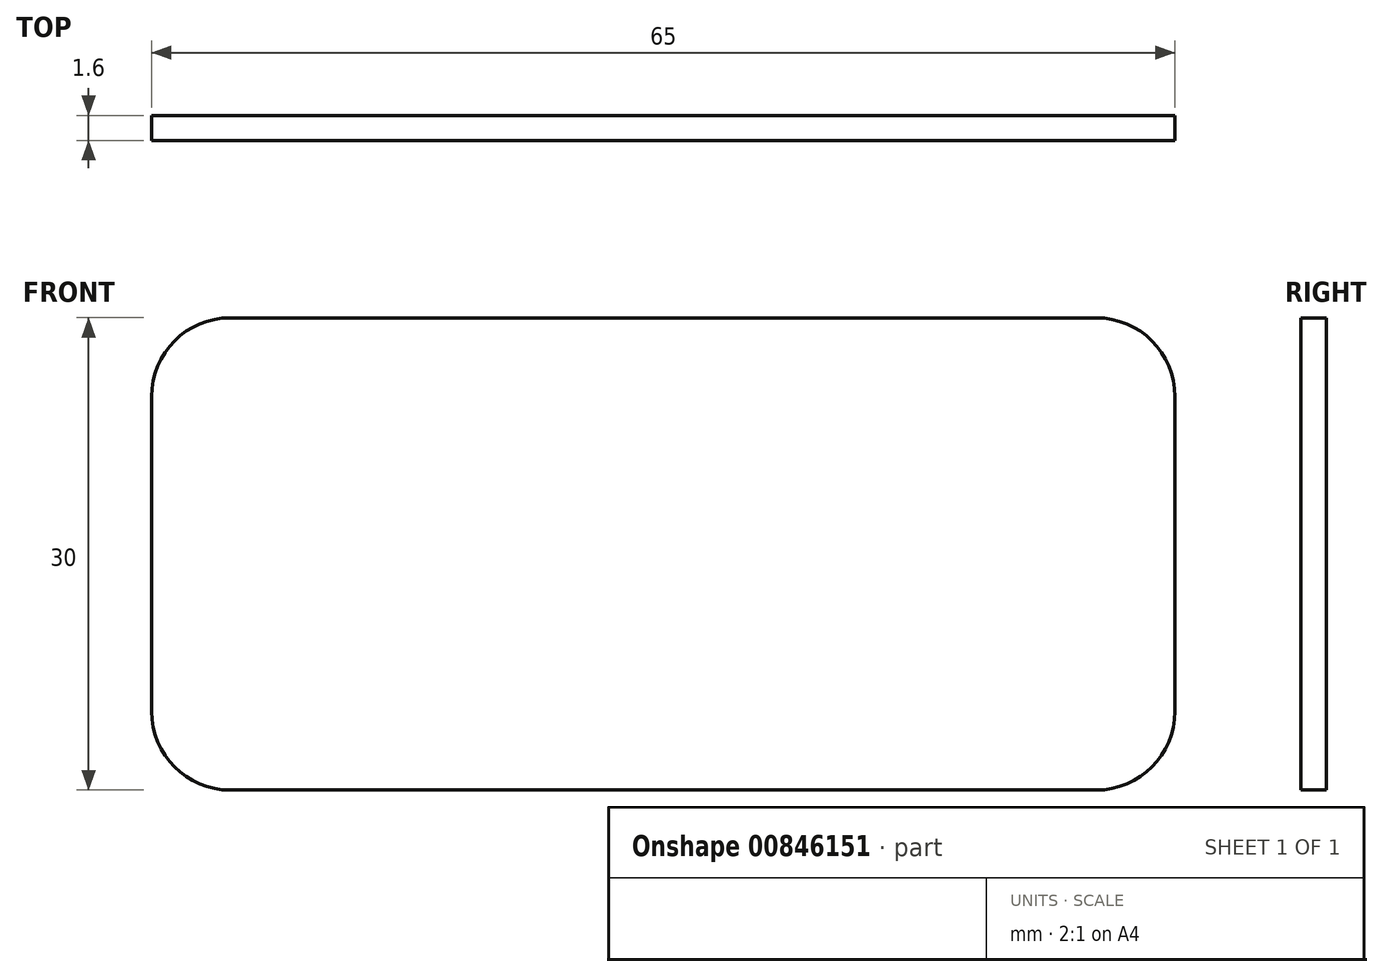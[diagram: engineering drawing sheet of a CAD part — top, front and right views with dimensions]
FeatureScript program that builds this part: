
annotation { "Feature Type Name" : "Feature", "Feature Type Description" : "" }
export const myFeature = defineFeature(function(context is Context, id is Id, definition is map)
    precondition{}
    {
        {
            var Q0;
            Q0=qCreatedBy(makeId("Front.planeOp"),FACE);
            var sketch = newSketch(context, id + "F0", { "sketchPlane" : qUnion([Q0])});
            skLineSegment(sketch, "E0.bottom", {"start": v(-11.3, 14.27) * mm, "end": v(43.7, 14.27) * mm});
            skLineSegment(sketch, "E0.top", {"start": v(-11.3, -15.73) * mm, "end": v(43.7, -15.73) * mm});
            skLineSegment(sketch, "E0.left", {"start": v(-16.3, 9.27) * mm, "end": v(-16.3, -10.73) * mm});
            skLineSegment(sketch, "E0.right", {"start": v(48.7, 9.27) * mm, "end": v(48.7, -10.73) * mm});
            skPoint(sketch, "E1.visualSharp", {"position": v(-16.3, 14.27) * mm});
            skArc(sketch, "E1.filletArc", {"start": v(-11.3, 14.27) * mm, "mid": v(-14.83, 12.8) * mm, "end": v(-16.3, 9.27) * mm});
            skPoint(sketch, "E2.visualSharp", {"position": v(48.7, 14.27) * mm});
            skArc(sketch, "E2.filletArc", {"start": v(48.7, 9.27) * mm, "mid": v(47.24, 12.8) * mm, "end": v(43.7, 14.27) * mm});
            skPoint(sketch, "E3.visualSharp", {"position": v(48.7, -15.73) * mm});
            skArc(sketch, "E3.filletArc", {"start": v(43.7, -15.73) * mm, "mid": v(47.24, -14.27) * mm, "end": v(48.7, -10.73) * mm});
            skPoint(sketch, "E4.visualSharp", {"position": v(-16.3, -15.73) * mm});
            skArc(sketch, "E4.filletArc", {"start": v(-16.3, -10.73) * mm, "mid": v(-14.83, -14.27) * mm, "end": v(-11.3, -15.73) * mm});
            skSolve(sketch);
        }
        {
            var Q0;
            Q0=makeQuery(id+"F0.imprint","IMPRINT",FACE,{"disambiguationData":[TD([[makeQuery(id+"F0.imprint","IMPRINT",EDGE,{"derivedFrom":sQuery(id+"F0.wireOp",EDGE,"E0.bottom")}),-1.0]])]});
            extrude(context, id + "F1", {"entities" : qUnion([Q0]), "depth" : 1.6 * mm, "offsetDistance" : 25 * mm});
        }
    });
